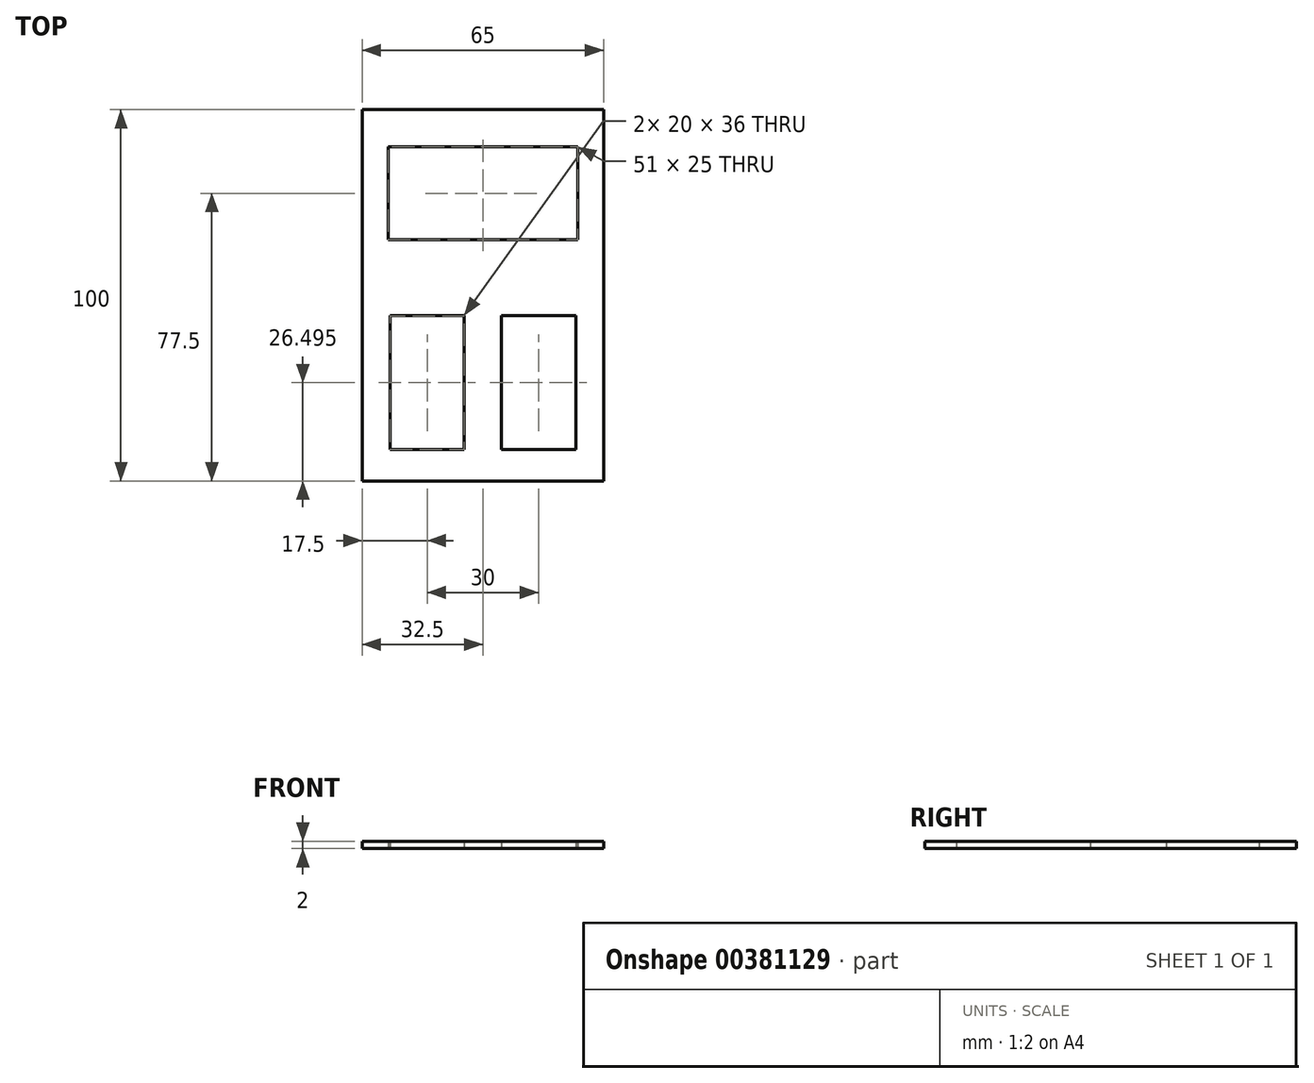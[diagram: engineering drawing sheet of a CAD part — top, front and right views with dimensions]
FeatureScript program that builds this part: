
annotation { "Feature Type Name" : "Feature", "Feature Type Description" : "" }
export const myFeature = defineFeature(function(context is Context, id is Id, definition is map)
    precondition{}
    {
        {
            var Q0;
            Q0=qCreatedBy(makeId("Top.planeOp"),FACE);
            var sketch = newSketch(context, id + "F0", { "sketchPlane" : qUnion([Q0])});
            skLineSegment(sketch, "E0.bottom", {"start": v(32.5, -50) * mm, "end": v(-32.5, -50) * mm});
            skLineSegment(sketch, "E0.top", {"start": v(32.5, 50) * mm, "end": v(-32.5, 50) * mm});
            skLineSegment(sketch, "E0.left", {"start": v(32.5, -50) * mm, "end": v(32.5, 50) * mm});
            skLineSegment(sketch, "E0.right", {"start": v(-32.5, -50) * mm, "end": v(-32.5, 50) * mm});
            skPoint(sketch, "E0.middle", {"position": v(0, 0) * mm});
            skLineSegment(sketch, "E1.bottom", {"start": v(-25.5, 40) * mm, "end": v(25.5, 40) * mm});
            skLineSegment(sketch, "E1.top", {"start": v(-25.5, 15) * mm, "end": v(25.5, 15) * mm});
            skLineSegment(sketch, "E1.left", {"start": v(-25.5, 40) * mm, "end": v(-25.5, 15) * mm});
            skLineSegment(sketch, "E1.right", {"start": v(25.5, 40) * mm, "end": v(25.5, 15) * mm});
            skLineSegment(sketch, "E2.bottom", {"start": v(-25, -5.5) * mm, "end": v(-5, -5.5) * mm});
            skLineSegment(sketch, "E2.top", {"start": v(-25, -41.5) * mm, "end": v(-5, -41.5) * mm});
            skLineSegment(sketch, "E2.left", {"start": v(-25, -5.5) * mm, "end": v(-25, -41.5) * mm});
            skLineSegment(sketch, "E2.right", {"start": v(-5, -5.5) * mm, "end": v(-5, -41.5) * mm});
            skLineSegment(sketch, "E3.bottom", {"start": v(5, -5.5) * mm, "end": v(25, -5.5) * mm});
            skLineSegment(sketch, "E3.top", {"start": v(5, -41.5) * mm, "end": v(25, -41.5) * mm});
            skLineSegment(sketch, "E3.left", {"start": v(5, -5.5) * mm, "end": v(5, -41.5) * mm});
            skLineSegment(sketch, "E3.right", {"start": v(25, -5.5) * mm, "end": v(25, -41.5) * mm});
            skSolve(sketch);
        }
        {
            var Q0;
            Q0=makeQuery(id+"F0.imprint","IMPRINT",FACE,{"disambiguationData":[TD([[makeQuery(id+"F0.imprint","IMPRINT",EDGE,{"derivedFrom":sQuery(id+"F0.wireOp",EDGE,"E0.bottom")}),-1.0]])]});
            extrude(context, id + "F1", {"entities" : qUnion([Q0]), "depth" : 2 * mm});
        }
    });
